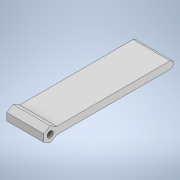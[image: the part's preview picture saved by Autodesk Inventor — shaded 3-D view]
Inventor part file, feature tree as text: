
AUTODESK INVENTOR PART (.ipt)
format: ipt  version: 2020 (Build 240168000, 168)  size: 123,392 bytes
history: native  units: in
note: dims shown in document units (in); Inventor stores cm internally (conversion verified against a paired STEP export)
features: extrude x2, sketch x2, plane x1
ambient origin geometry x8: Origin, YZ Plane, XZ Plane, XY Plane, X Axis, Y Axis, Z Axis, Center Point
bodies: Solid1 (feature_tree)
feature tree (5):
  extrude  "Extrusion1"  Depth=2.7559in
  plane  "Work Plane1"
  extrude  "Extrusion2"  Depth=0.7874in
  sketch  "Sketch1"  dims[d0=0.1575in d1=2.7559in]
  sketch  "Sketch2"  dims[d2=0.1299in d3=0.7874in d4=0.0in d5=0.0787in d6=0.7874in d7=0.0in]
